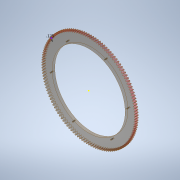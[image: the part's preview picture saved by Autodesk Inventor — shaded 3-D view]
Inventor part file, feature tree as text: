
AUTODESK INVENTOR PART (.ipt)
format: ipt  version: 2020 (Build 240168000, 168)  size: 2,175,488 bytes
history: native  units: mm (DEFAULTED — no unit token found)
features: sketch x3, hole x2, extrude x1, pattern_circular x1, projected_geometry x1, other x1
ambient origin geometry x8: Origin, YZ Plane, XZ Plane, XY Plane, X Axis, Y Axis, Z Axis, Center Point
bodies: Solid1 (feature_tree)
feature tree (9):
  extrude  "Extrusion1"  Depth=25.4mm
  hole  "Hole1"  [1 undecoded]
  hole  "Hole2"  [1 undecoded]
  pattern_circular  "Circular Pattern1"  [2 undecoded]
  sketch  "Sketch1"  dims[d0=260.35mm d1=9.652mm d2=9.525mm d3=6.35mm d4=14.3117mm d5=25.4mm d6=20.594885mm d7=273.5mm]
  sketch  "Sketch2"  dims[d8=3.9624mm d9=9.652mm d10=11.1252mm d11=6.35mm d12=14.0mm d13=13.6144mm d14=20.594885mm d15=60.0mm d16=62.831853mm]
  sketch  "Sketch3"  dims[d18=3.175mm d19=0.0mm d17=19.05mm d21=25.4mm d22=25.4mm d23=25.4mm d24=3.81mm d25=6.35mm d26=9.525mm d27=820.0mm d28=19.05mm d29=1180.0mm d30=1.5875mm d31=19.05mm d32=9.525mm]
  projected_geometry  "Projected Loop1"
  other  "Pattern10DP 130T Gear"
note: 4 required parameter values undecoded (feature->parameter linkage not recoverable at this tier; creation-order binding heuristic only, values carry confidence <= 0.55)
